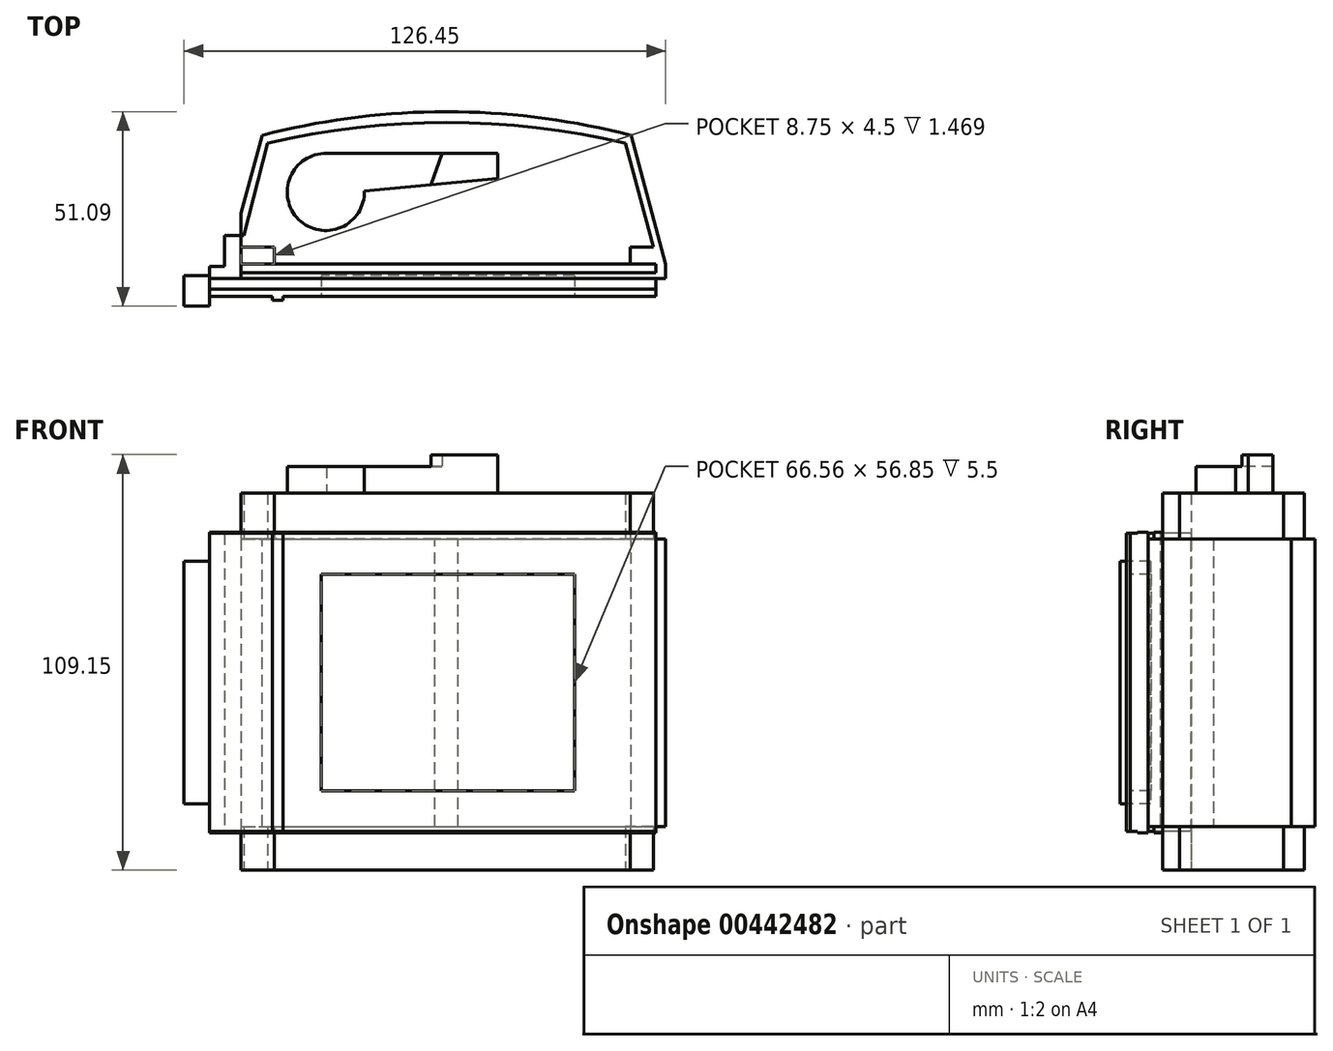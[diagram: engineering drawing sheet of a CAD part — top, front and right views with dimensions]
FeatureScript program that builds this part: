
annotation { "Feature Type Name" : "Feature", "Feature Type Description" : "" }
export const myFeature = defineFeature(function(context is Context, id is Id, definition is map)
    precondition{}
    {
        {
            var Q0;
            Q0=qCreatedBy(makeId("Front.planeOp"),FACE);
            var sketch = newSketch(context, id + "F0", { "sketchPlane" : qUnion([Q0])});
            skLineSegment(sketch, "E0.bottom", {"start": v(58.63, 39.17) * mm, "end": v(-58.62, 39.17) * mm});
            skLineSegment(sketch, "E0.top", {"start": v(58.63, -39.17) * mm, "end": v(-58.63, -39.17) * mm});
            skLineSegment(sketch, "E0.left", {"start": v(58.63, 39.17) * mm, "end": v(58.63, -39.18) * mm});
            skLineSegment(sketch, "E0.right", {"start": v(-58.63, 39.17) * mm, "end": v(-58.63, -39.17) * mm});
            skPoint(sketch, "E0.middle", {"position": v(0, 0) * mm});
            skLineSegment(sketch, "E1.bottom", {"start": v(-39.38, 39.17) * mm, "end": v(-41.87, 39.17) * mm});
            skLineSegment(sketch, "E1.top", {"start": v(-39.38, -39.17) * mm, "end": v(-41.87, -39.17) * mm});
            skLineSegment(sketch, "E1.left", {"start": v(-39.38, 39.18) * mm, "end": v(-39.38, -39.17) * mm});
            skLineSegment(sketch, "E1.right", {"start": v(-41.87, 39.18) * mm, "end": v(-41.87, -39.17) * mm});
            skSolve(sketch);
        }
        {
            var Q0;
            Q0=qSketchRegion(id+"F0",true);
            extrude(context, id + "F1", {"entities" : qUnion([Q0]), "depth" : 4.75 * mm});
        }
        {
            var Q0;
            Q0=makeQuery(id+"F1.opExtrude","CAP_FACE",FACE,{"disambiguationData":[OSD([sQuery(id+"F0.wireOp",EDGE,"E0.bottom"),sQuery(id+"F0.wireOp",EDGE,"E0.top"),sQuery(id+"F0.wireOp",EDGE,"E0.left"),sQuery(id+"F0.wireOp",EDGE,"E0.right"),sQuery(id+"F0.wireOp",EDGE,"E1.bottom"),sQuery(id+"F0.wireOp",EDGE,"E1.top")])],"isStart":false});
            var sketch = newSketch(context, id + "F2", { "sketchPlane" : qUnion([Q0])});
            skLineSegment(sketch, "E2.bottom", {"start": v(-42.12, 39.17) * mm, "end": v(-39.38, 39.17) * mm});
            skLineSegment(sketch, "E2.top", {"start": v(-42.12, -39.17) * mm, "end": v(-39.38, -39.17) * mm});
            skLineSegment(sketch, "E2.left", {"start": v(-42.12, 39.17) * mm, "end": v(-42.12, -39.17) * mm});
            skLineSegment(sketch, "E2.right", {"start": v(-39.38, 39.17) * mm, "end": v(-39.38, -39.17) * mm});
            skSolve(sketch);
        }
        {
            var Q0;
            Q0=qSketchRegion(id+"F2",true);
            extrude(context, id + "F3", {"entities" : qUnion([Q0]), "operationType" : NewBodyOperationType.ADD, "depth" : 1 * mm});
        }
        {
            var Q0;
            {var subQ0=sQuery(id+"F0.wireOp",EDGE,"E0.left");var subQ1=sQuery(id+"F0.wireOp",EDGE,"E1.top");var subQ2=sQuery(id+"F0.wireOp",EDGE,"E0.top");var subQ3=sQuery(id+"F0.wireOp",EDGE,"E1.bottom");var subQ4=sQuery(id+"F0.wireOp",EDGE,"E0.bottom");Q0=makeQuery(id+"F3.boolean.opBoolean","SPLIT",FACE,{"disambiguationData":[TD([makeQuery(id+"F1.opExtrude","SWEPT_FACE",FACE,{"disambiguationData":[OSD([subQ0])]})])],"derivedFrom":makeQuery(id+"F1.opExtrude","CAP_FACE",FACE,{"disambiguationData":[OSD([subQ4,subQ2,subQ0,sQuery(id+"F0.wireOp",EDGE,"E0.right"),subQ3,subQ1])],"isStart":false})});}
            var sketch = newSketch(context, id + "F4", { "sketchPlane" : qUnion([Q0])});
            skLineSegment(sketch, "E3.bottom", {"start": v(37.23, 28.42) * mm, "end": v(-29.34, 28.42) * mm});
            skLineSegment(sketch, "E3.top", {"start": v(37.23, -28.42) * mm, "end": v(-29.33, -28.42) * mm});
            skLineSegment(sketch, "E3.left", {"start": v(37.23, 28.42) * mm, "end": v(37.23, -28.42) * mm});
            skLineSegment(sketch, "E3.right", {"start": v(-29.34, 28.42) * mm, "end": v(-29.33, -28.42) * mm});
            skSolve(sketch);
        }
        {
            var Q0;
            Q0=qSketchRegion(id+"F4",true);
            extrude(context, id + "F5", {"entities" : qUnion([Q0]), "operationType" : NewBodyOperationType.REMOVE, "oppositeDirection" : true, "depth" : 25 * mm});
        }
        {
            var Q0;
            Q0=makeQuery(id+"F1.opExtrude","CAP_FACE",FACE,{"disambiguationData":[OSD([sQuery(id+"F0.wireOp",EDGE,"E0.bottom"),sQuery(id+"F0.wireOp",EDGE,"E0.top"),sQuery(id+"F0.wireOp",EDGE,"E0.left"),sQuery(id+"F0.wireOp",EDGE,"E0.right"),sQuery(id+"F0.wireOp",EDGE,"E1.bottom"),sQuery(id+"F0.wireOp",EDGE,"E1.top")])],"isStart":true});
            var sketch = newSketch(context, id + "F6", { "sketchPlane" : qUnion([Q0])});
            skLineSegment(sketch, "E4.bottom", {"start": v(58.63, 39.5) * mm, "end": v(-58.63, 39.5) * mm});
            skLineSegment(sketch, "E4.top", {"start": v(58.63, -39.5) * mm, "end": v(-58.63, -39.5) * mm});
            skLineSegment(sketch, "E4.left", {"start": v(58.63, 39.5) * mm, "end": v(58.63, -39.5) * mm});
            skLineSegment(sketch, "E4.right", {"start": v(-58.63, 39.5) * mm, "end": v(-58.63, -39.5) * mm});
            skPoint(sketch, "E4.middle", {"position": v(0, 0) * mm});
            skSolve(sketch);
        }
        {
            var Q0;
            Q0=qSketchRegion(id+"F6",true);
            extrude(context, id + "F7", {"entities" : qUnion([Q0]), "operationType" : NewBodyOperationType.ADD, "oppositeDirection" : true, "depth" : 2.86 * mm});
        }
        {
            var Q0;
            {var subQ0=sQuery(id+"F0.wireOp",EDGE,"E0.right");var subQ1=sQuery(id+"F0.wireOp",EDGE,"E1.top");var subQ2=sQuery(id+"F0.wireOp",EDGE,"E0.top");var subQ3=sQuery(id+"F0.wireOp",EDGE,"E1.bottom");var subQ4=sQuery(id+"F0.wireOp",EDGE,"E0.bottom");Q0=makeQuery(id+"F3.boolean.opBoolean","SPLIT",FACE,{"disambiguationData":[TD([makeQuery(id+"F1.opExtrude","SWEPT_FACE",FACE,{"disambiguationData":[OSD([subQ0])]})])],"derivedFrom":makeQuery(id+"F1.opExtrude","CAP_FACE",FACE,{"disambiguationData":[OSD([subQ4,subQ2,sQuery(id+"F0.wireOp",EDGE,"E0.left"),subQ0,subQ3,subQ1])],"isStart":false})});}
            var sketch = newSketch(context, id + "F8", { "sketchPlane" : qUnion([Q0])});
            skLineSegment(sketch, "E5.bottom", {"start": v(-58.62, 39.17) * mm, "end": v(-54.72, 39.17) * mm});
            skLineSegment(sketch, "E5.top", {"start": v(-58.62, -39.17) * mm, "end": v(-54.72, -39.17) * mm});
            skLineSegment(sketch, "E5.left", {"start": v(-58.62, 39.17) * mm, "end": v(-58.62, -39.17) * mm});
            skLineSegment(sketch, "E5.right", {"start": v(-54.72, 39.17) * mm, "end": v(-54.72, -39.17) * mm});
            skSolve(sketch);
        }
        {
            var Q0;
            Q0=qSketchRegion(id+"F8",true);
            extrude(context, id + "F9", {"entities" : qUnion([Q0]), "operationType" : NewBodyOperationType.ADD, "oppositeDirection" : true, "depth" : 7.9 * mm});
        }
        {
            var Q0;
            {var subQ0=sQuery(id+"F0.wireOp",EDGE,"E0.right");var subQ1=sQuery(id+"F0.wireOp",EDGE,"E1.top");var subQ2=sQuery(id+"F0.wireOp",EDGE,"E0.top");var subQ3=sQuery(id+"F0.wireOp",EDGE,"E1.bottom");var subQ4=sQuery(id+"F0.wireOp",EDGE,"E0.bottom");Q0=makeQuery(id+"F3.boolean.opBoolean","SPLIT",FACE,{"disambiguationData":[TD([makeQuery(id+"F1.opExtrude","SWEPT_FACE",FACE,{"disambiguationData":[OSD([subQ0])]})])],"derivedFrom":makeQuery(id+"F1.opExtrude","CAP_FACE",FACE,{"disambiguationData":[OSD([subQ4,subQ2,sQuery(id+"F0.wireOp",EDGE,"E0.left"),subQ0,subQ3,subQ1])],"isStart":false})});}
            var sketch = newSketch(context, id + "F10", { "sketchPlane" : qUnion([Q0])});
            skLineSegment(sketch, "E6.bottom", {"start": v(-58.62, 39.17) * mm, "end": v(-50.31, 39.17) * mm});
            skLineSegment(sketch, "E6.top", {"start": v(-58.62, -39.17) * mm, "end": v(-50.31, -39.17) * mm});
            skLineSegment(sketch, "E6.left", {"start": v(-58.62, 39.17) * mm, "end": v(-58.62, -39.17) * mm});
            skLineSegment(sketch, "E6.right", {"start": v(-50.31, 39.17) * mm, "end": v(-50.31, -39.17) * mm});
            skSolve(sketch);
        }
        {
            var Q0;
            Q0=qSketchRegion(id+"F10",true);
            extrude(context, id + "F11", {"entities" : qUnion([Q0]), "operationType" : NewBodyOperationType.ADD, "oppositeDirection" : true, "depth" : 6.5 * mm});
        }
        {
            var Q0;
            Q0=makeQuery(id+"F7.boolean.opBoolean","MERGE",FACE,{"derivedFrom":[makeQuery(id+"F1.opExtrude","CAP_FACE",FACE,{"disambiguationData":[OSD([sQuery(id+"F0.wireOp",EDGE,"E0.bottom"),sQuery(id+"F0.wireOp",EDGE,"E0.top"),sQuery(id+"F0.wireOp",EDGE,"E0.left"),sQuery(id+"F0.wireOp",EDGE,"E0.right"),sQuery(id+"F0.wireOp",EDGE,"E1.bottom"),sQuery(id+"F0.wireOp",EDGE,"E1.top")])],"isStart":true}),makeQuery(id+"F7.opExtrude","CAP_FACE",FACE,{"disambiguationData":[OSD([sQuery(id+"F6.wireOp",EDGE,"E4.bottom"),sQuery(id+"F6.wireOp",EDGE,"E4.top"),sQuery(id+"F6.wireOp",EDGE,"E4.left"),sQuery(id+"F6.wireOp",EDGE,"E4.right")])],"isStart":true})]});
            var sketch = newSketch(context, id + "F12", { "sketchPlane" : qUnion([Q0])});
            skLineSegment(sketch, "E7.left", {"start": v(-61.13, 37.7) * mm, "end": v(-61.13, -37.83) * mm});
            skLineSegment(sketch, "E8", {"start": v(50.31, 37.7) * mm, "end": v(50.31, -37.83) * mm});
            skLineSegment(sketch, "E9", {"start": v(50.31, -37.83) * mm, "end": v(-61.13, -37.83) * mm});
            skLineSegment(sketch, "E10", {"start": v(50.31, 37.7) * mm, "end": v(-61.13, 37.7) * mm});
            skSolve(sketch);
        }
        {
            var Q0;
            Q0=qSketchRegion(id+"F12",true);
            extrude(context, id + "F13", {"entities" : qUnion([Q0]), "operationType" : NewBodyOperationType.ADD, "depth" : 1.5 * mm});
        }
        {
            var Q0;
            Q0=makeQuery(id+"F11.opExtrude","CAP_FACE",FACE,{"disambiguationData":[OSD([sQuery(id+"F10.wireOp",EDGE,"E6.bottom"),sQuery(id+"F10.wireOp",EDGE,"E6.top"),sQuery(id+"F10.wireOp",EDGE,"E6.left"),sQuery(id+"F10.wireOp",EDGE,"E6.right")])],"isStart":false});
            var sketch = newSketch(context, id + "F14", { "sketchPlane" : qUnion([Q0])});
            skLineSegment(sketch, "E11.bottom", {"start": v(54.72, 39.17) * mm, "end": v(50.31, 39.17) * mm});
            skLineSegment(sketch, "E11.top", {"start": v(54.72, -39.17) * mm, "end": v(50.31, -39.17) * mm});
            skLineSegment(sketch, "E11.left", {"start": v(54.72, 39.17) * mm, "end": v(54.72, -39.17) * mm});
            skLineSegment(sketch, "E11.right", {"start": v(50.31, 39.17) * mm, "end": v(50.31, -39.17) * mm});
            skSolve(sketch);
        }
        {
            var Q0;
            Q0=qSketchRegion(id+"F14",true);
            extrude(context, id + "F15", {"entities" : qUnion([Q0]), "operationType" : NewBodyOperationType.ADD, "depth" : 9.5 * mm});
        }
        {
            var Q0;
            Q0=makeQuery(id+"F13.opExtrude","CAP_FACE",FACE,{"disambiguationData":[OSD([sQuery(id+"F12.wireOp",EDGE,"E7.left"),sQuery(id+"F12.wireOp",EDGE,"E8"),sQuery(id+"F12.wireOp",EDGE,"E9"),sQuery(id+"F12.wireOp",EDGE,"E10")])],"isStart":false});
            var sketch = newSketch(context, id + "F16", { "sketchPlane" : qUnion([Q0])});
            skLineSegment(sketch, "E12", {"start": v(-58.63, 39.5) * mm, "end": v(50.31, 39.5) * mm});
            skLineSegment(sketch, "E13", {"start": v(50.31, 39.5) * mm, "end": v(50.31, -39.5) * mm});
            skLineSegment(sketch, "E14", {"start": v(50.31, -39.5) * mm, "end": v(-58.63, -39.5) * mm});
            skLineSegment(sketch, "E15", {"start": v(-58.63, -39.5) * mm, "end": v(-58.63, -37.83) * mm});
            skLineSegment(sketch, "E16", {"start": v(-58.63, -37.83) * mm, "end": v(-61.13, -37.83) * mm});
            skLineSegment(sketch, "E17", {"start": v(-61.13, -37.83) * mm, "end": v(-61.13, 37.7) * mm});
            skLineSegment(sketch, "E18", {"start": v(-61.13, 37.7) * mm, "end": v(-58.63, 37.7) * mm});
            skLineSegment(sketch, "E19", {"start": v(-58.63, 37.7) * mm, "end": v(-58.63, 39.5) * mm});
            skSolve(sketch);
        }
        {
            var Q0;
            Q0=qSketchRegion(id+"F16",true);
            extrude(context, id + "F17", {"entities" : qUnion([Q0]), "operationType" : NewBodyOperationType.ADD, "depth" : 2.25 * mm});
        }
        {
            var Q0;
            Q0=makeQuery(id+"F17.opExtrude","CAP_FACE",FACE,{"disambiguationData":[OSD([sQuery(id+"F16.wireOp",EDGE,"E12"),sQuery(id+"F16.wireOp",EDGE,"E13"),sQuery(id+"F16.wireOp",EDGE,"E14"),sQuery(id+"F16.wireOp",EDGE,"E15"),sQuery(id+"F16.wireOp",EDGE,"E16"),sQuery(id+"F16.wireOp",EDGE,"E17"),sQuery(id+"F16.wireOp",EDGE,"E18"),sQuery(id+"F16.wireOp",EDGE,"E19")])],"isStart":false});
            var sketch = newSketch(context, id + "F18", { "sketchPlane" : qUnion([Q0])});
            skLineSegment(sketch, "E20", {"start": v(-61.13, 37.7) * mm, "end": v(-58.63, 37.7) * mm});
            skLineSegment(sketch, "E21", {"start": v(-58.63, -37.83) * mm, "end": v(-61.13, -37.83) * mm});
            skLineSegment(sketch, "E22", {"start": v(-61.13, -37.83) * mm, "end": v(-61.13, 37.7) * mm});
            skLineSegment(sketch, "E23", {"start": v(-58.63, 37.7) * mm, "end": v(50.31, 37.7) * mm});
            skLineSegment(sketch, "E24", {"start": v(-58.63, -37.83) * mm, "end": v(50.31, -37.83) * mm});
            skLineSegment(sketch, "E25", {"start": v(50.31, -37.83) * mm, "end": v(50.31, 37.7) * mm});
            skSolve(sketch);
        }
        {
            var Q0;
            Q0=qSketchRegion(id+"F18",true);
            extrude(context, id + "F19", {"entities" : qUnion([Q0]), "operationType" : NewBodyOperationType.ADD, "depth" : 40 * mm});
        }
        {
            var Q0;
            Q0=makeQuery(id+"F19.boolean.opBoolean","MERGE",FACE,{"derivedFrom":[makeQuery(id+"F17.boolean.opBoolean","MERGE",FACE,{"derivedFrom":[makeQuery(id+"F13.opExtrude","SWEPT_FACE",FACE,{"disambiguationData":[OSD([sQuery(id+"F12.wireOp",EDGE,"E10")])]}),makeQuery(id+"F17.opExtrude","SWEPT_FACE",FACE,{"disambiguationData":[OSD([sQuery(id+"F16.wireOp",EDGE,"E18")])]})]}),makeQuery(id+"F19.opExtrude","SWEPT_FACE",FACE,{"disambiguationData":[OSD([sQuery(id+"F18.wireOp",EDGE,"E20"),sQuery(id+"F18.wireOp",EDGE,"E23")])]})]});
            var sketch = newSketch(context, id + "F20", { "sketchPlane" : qUnion([Q0])});
            skLineSegment(sketch, "E26", {"start": v(61.13, 3.75) * mm, "end": v(52.07, 37.56) * mm});
            skLineSegment(sketch, "E27", {"start": v(52.07, 37.56) * mm, "end": v(-44.84, 37.56) * mm, "construction": true});
            skLineSegment(sketch, "E28", {"start": v(-44.84, 37.56) * mm, "end": v(-51.88, 11.25) * mm});
            skLineSegment(sketch, "E29", {"start": v(-51.88, 11.25) * mm, "end": v(-55.7, 49.97) * mm});
            skLineSegment(sketch, "E30", {"start": v(-55.7, 49.97) * mm, "end": v(71.24, 49.97) * mm});
            skLineSegment(sketch, "E31", {"start": v(71.24, 49.97) * mm, "end": v(61.13, 3.75) * mm});
            skLineSegment(sketch, "E32", {"start": v(-51.88, 11.25) * mm, "end": v(59.12, 11.25) * mm, "construction": true});
            skLineSegment(sketch, "E33", {"start": v(3.62, 11.25) * mm, "end": v(3.62, 37.56) * mm, "construction": true});
            skArc(sketch, "E34", {"start": v(52.07, 37.56) * mm, "mid": v(3.62, 43.77) * mm, "end": v(-44.84, 37.56) * mm});
            skSolve(sketch);
        }
        {
            var Q0;
            Q0=qSketchRegion(id+"F20",true);
            extrude(context, id + "F21", {"entities" : qUnion([Q0]), "operationType" : NewBodyOperationType.REMOVE, "oppositeDirection" : true, "depth" : 95.3 * mm});
        }
        {
            var Q0;
            Q0=makeQuery(id+"F19.boolean.opBoolean","MERGE",FACE,{"derivedFrom":[makeQuery(id+"F17.boolean.opBoolean","MERGE",FACE,{"derivedFrom":[makeQuery(id+"F13.opExtrude","SWEPT_FACE",FACE,{"disambiguationData":[OSD([sQuery(id+"F12.wireOp",EDGE,"E10")])]}),makeQuery(id+"F17.opExtrude","SWEPT_FACE",FACE,{"disambiguationData":[OSD([sQuery(id+"F16.wireOp",EDGE,"E18")])]})]}),makeQuery(id+"F19.opExtrude","SWEPT_FACE",FACE,{"disambiguationData":[OSD([sQuery(id+"F18.wireOp",EDGE,"E20"),sQuery(id+"F18.wireOp",EDGE,"E23")])]})]});
            var sketch = newSketch(context, id + "F22", { "sketchPlane" : qUnion([Q0])});
            skLineSegment(sketch, "E35", {"start": v(-41.56, 3.75) * mm, "end": v(-41.56, 8.25) * mm, "construction": true});
            skLineSegment(sketch, "E36", {"start": v(51.92, 8.25) * mm, "end": v(51.92, 3.75) * mm, "construction": true});
            skLineSegment(sketch, "E37", {"start": v(-50.31, 8.25) * mm, "end": v(-41.56, 8.25) * mm, "construction": true});
            skLineSegment(sketch, "E38", {"start": v(50.6, 35.56) * mm, "end": v(57.92, 8.25) * mm, "construction": true});
            skLineSegment(sketch, "E39", {"start": v(51.92, 8.25) * mm, "end": v(57.92, 8.25) * mm, "construction": true});
            skArc(sketch, "E40", {"start": v(50.6, 35.56) * mm, "mid": v(3.63, 40.98) * mm, "end": v(-43.35, 35.56) * mm, "construction": true});
            skLineSegment(sketch, "E41", {"start": v(-41.57, 3.75) * mm, "end": v(51.92, 3.75) * mm, "construction": true});
            skLineSegment(sketch, "E42", {"start": v(-50.31, 8.25) * mm, "end": v(-41.56, 8.25) * mm});
            skLineSegment(sketch, "E43", {"start": v(-41.56, 8.25) * mm, "end": v(-41.56, 3.75) * mm});
            skLineSegment(sketch, "E44", {"start": v(-41.57, 3.75) * mm, "end": v(51.92, 3.75) * mm});
            skLineSegment(sketch, "E45", {"start": v(51.92, 3.75) * mm, "end": v(51.92, 8.25) * mm});
            skLineSegment(sketch, "E46", {"start": v(51.92, 8.25) * mm, "end": v(57.92, 8.25) * mm});
            skLineSegment(sketch, "E47", {"start": v(57.92, 8.25) * mm, "end": v(50.6, 35.56) * mm});
            skArc(sketch, "E48", {"start": v(50.6, 35.56) * mm, "mid": v(3.63, 40.94) * mm, "end": v(-43.35, 35.56) * mm});
            skLineSegment(sketch, "E49", {"start": v(-50.31, 8.25) * mm, "end": v(-50.31, 11.25) * mm});
            skLineSegment(sketch, "E50", {"start": v(-50.31, 11.25) * mm, "end": v(-49.55, 11.25) * mm});
            skLineSegment(sketch, "E51", {"start": v(-49.55, 11.25) * mm, "end": v(-43.35, 35.56) * mm});
            skSolve(sketch);
        }
        {
            var Q0;
            Q0=qSketchRegion(id+"F22",true);
            extrude(context, id + "F23", {"entities" : qUnion([Q0]), "operationType" : NewBodyOperationType.ADD, "depth" : 12 * mm, "hasSecondDirection" : true, "secondDirectionOppositeDirection" : true, "secondDirectionDepth" : 87 * mm});
        }
        {
            var Q0;
            Q0=makeQuery(id+"F23.opExtrude","CAP_FACE",FACE,{"disambiguationData":[OSD([sQuery(id+"F22.wireOp",EDGE,"E42"),sQuery(id+"F22.wireOp",EDGE,"E43"),sQuery(id+"F22.wireOp",EDGE,"E44"),sQuery(id+"F22.wireOp",EDGE,"E45"),sQuery(id+"F22.wireOp",EDGE,"E46"),sQuery(id+"F22.wireOp",EDGE,"E47"),sQuery(id+"F22.wireOp",EDGE,"E48"),sQuery(id+"F22.wireOp",EDGE,"E49"),sQuery(id+"F22.wireOp",EDGE,"E50"),sQuery(id+"F22.wireOp",EDGE,"E51")])],"isStart":false});
            var sketch = newSketch(context, id + "F24", { "sketchPlane" : qUnion([Q0])});
            skCircle(sketch, "E52", {"center": v(-28.09, 22.68) * mm, "radius": 10.12 * mm});
            skLineSegment(sketch, "E53", {"start": v(-27.89, 32.8) * mm, "end": v(17.11, 32.8) * mm});
            skLineSegment(sketch, "E54", {"start": v(17.11, 32.8) * mm, "end": v(17.11, 26.3) * mm});
            skLineSegment(sketch, "E55", {"start": v(17.11, 26.3) * mm, "end": v(-17.97, 22.97) * mm});
            skSolve(sketch);
        }
        {
            var Q0;
            Q0=qSketchRegion(id+"F24",true);
            extrude(context, id + "F25", {"entities" : qUnion([Q0]), "operationType" : NewBodyOperationType.ADD, "depth" : 7 * mm});
        }
        {
            var Q0;
            Q0=makeQuery(id+"F25.opExtrude","CAP_FACE",FACE,{"disambiguationData":[OSD([sQuery(id+"F24.wireOp",EDGE,"E52"),sQuery(id+"F24.wireOp",EDGE,"E53"),sQuery(id+"F24.wireOp",EDGE,"E54"),sQuery(id+"F24.wireOp",EDGE,"E55")])],"isStart":false});
            var sketch = newSketch(context, id + "F26", { "sketchPlane" : qUnion([Q0])});
            skLineSegment(sketch, "E56", {"start": v(17.11, 32.8) * mm, "end": v(2.42, 32.8) * mm});
            skLineSegment(sketch, "E57", {"start": v(2.42, 32.8) * mm, "end": v(-0.43, 24.64) * mm});
            skLineSegment(sketch, "E58", {"start": v(-0.43, 24.64) * mm, "end": v(17.11, 26.3) * mm});
            skLineSegment(sketch, "E59", {"start": v(17.11, 26.3) * mm, "end": v(17.11, 32.8) * mm});
            skSolve(sketch);
        }
        {
            var Q0;
            Q0=qSketchRegion(id+"F26",true);
            extrude(context, id + "F27", {"entities" : qUnion([Q0]), "operationType" : NewBodyOperationType.ADD, "depth" : 3.15 * mm});
        }
        {
            var Q0;
            Q0=makeQuery(id+"F9.boolean.opBoolean","MERGE",FACE,{"derivedFrom":[makeQuery(id+"F7.boolean.opBoolean","MERGE",FACE,{"derivedFrom":[makeQuery(id+"F1.opExtrude","SWEPT_FACE",FACE,{"disambiguationData":[OSD([sQuery(id+"F0.wireOp",EDGE,"E0.right")])]}),makeQuery(id+"F7.opExtrude","SWEPT_FACE",FACE,{"disambiguationData":[OSD([sQuery(id+"F6.wireOp",EDGE,"E4.left")])]})]}),makeQuery(id+"F9.opExtrude","SWEPT_FACE",FACE,{"disambiguationData":[OSD([sQuery(id+"F8.wireOp",EDGE,"E5.left")])]})]});
            var sketch = newSketch(context, id + "F28", { "sketchPlane" : qUnion([Q0])});
            skLineSegment(sketch, "E60.bottom", {"start": v(-0.66, 31.87) * mm, "end": v(7.34, 31.87) * mm});
            skLineSegment(sketch, "E60.top", {"start": v(-0.66, -31.88) * mm, "end": v(7.34, -31.88) * mm});
            skLineSegment(sketch, "E60.left", {"start": v(-0.66, 31.87) * mm, "end": v(-0.66, -31.88) * mm});
            skLineSegment(sketch, "E60.right", {"start": v(7.34, 31.87) * mm, "end": v(7.34, -31.88) * mm});
            skSolve(sketch);
        }
        {
            var Q0;
            Q0=qSketchRegion(id+"F28",true);
            extrude(context, id + "F29", {"entities" : qUnion([Q0]), "operationType" : NewBodyOperationType.ADD, "depth" : 6.7 * mm});
        }
        {
            var Q0;
            {var subQ0=sQuery(id+"F0.wireOp",EDGE,"E0.left");var subQ1=sQuery(id+"F0.wireOp",EDGE,"E1.top");var subQ2=sQuery(id+"F0.wireOp",EDGE,"E0.top");var subQ3=sQuery(id+"F0.wireOp",EDGE,"E1.bottom");var subQ4=sQuery(id+"F0.wireOp",EDGE,"E0.bottom");Q0=makeQuery(id+"F3.boolean.opBoolean","SPLIT",FACE,{"disambiguationData":[TD([makeQuery(id+"F1.opExtrude","SWEPT_FACE",FACE,{"disambiguationData":[OSD([subQ0])]})])],"derivedFrom":makeQuery(id+"F1.opExtrude","CAP_FACE",FACE,{"disambiguationData":[OSD([subQ4,subQ2,subQ0,sQuery(id+"F0.wireOp",EDGE,"E0.right"),subQ3,subQ1])],"isStart":false})});}
            var sketch = newSketch(context, id + "F30", { "sketchPlane" : qUnion([Q0])});
            skLineSegment(sketch, "E61.bottom", {"start": v(-29.34, 28.42) * mm, "end": v(37.23, 28.42) * mm});
            skLineSegment(sketch, "E61.top", {"start": v(-29.34, -28.42) * mm, "end": v(37.23, -28.42) * mm});
            skLineSegment(sketch, "E61.left", {"start": v(-29.34, 28.42) * mm, "end": v(-29.34, -28.42) * mm});
            skLineSegment(sketch, "E61.right", {"start": v(37.23, 28.42) * mm, "end": v(37.23, -28.42) * mm});
            skSolve(sketch);
        }
        {
            var Q0;
            Q0=qSketchRegion(id+"F30",true);
            extrude(context, id + "F31", {"entities" : qUnion([Q0]), "operationType" : NewBodyOperationType.REMOVE, "oppositeDirection" : true, "depth" : 5.5 * mm});
        }
    });
